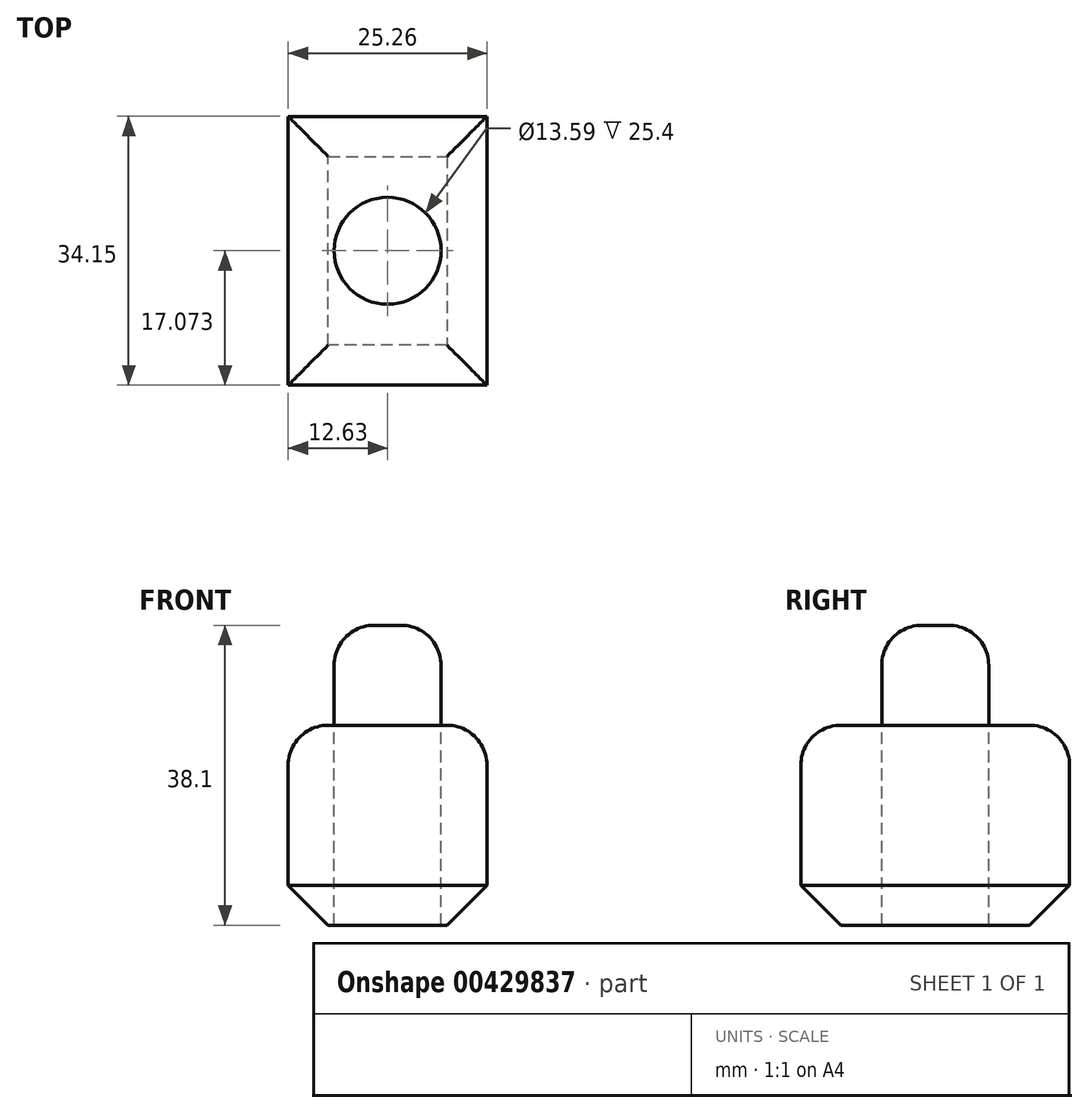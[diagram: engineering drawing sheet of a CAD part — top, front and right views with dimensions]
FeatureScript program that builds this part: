
annotation { "Feature Type Name" : "Feature", "Feature Type Description" : "" }
export const myFeature = defineFeature(function(context is Context, id is Id, definition is map)
    precondition{}
    {
        {
            var Q0;
            Q0=qCreatedBy(makeId("Top.planeOp"),FACE);
            var sketch = newSketch(context, id + "F0", { "sketchPlane" : qUnion([Q0])});
            skLineSegment(sketch, "E0", {"start": v(0, 0) * mm, "end": v(0, 34.15) * mm});
            skLineSegment(sketch, "E1", {"start": v(0, 34.15) * mm, "end": v(25.26, 34.15) * mm});
            skLineSegment(sketch, "E2", {"start": v(25.26, 34.15) * mm, "end": v(25.26, 0) * mm});
            skLineSegment(sketch, "E3", {"start": v(25.26, 0) * mm, "end": v(0, 0) * mm});
            skCircle(sketch, "E4", {"center": v(12.63, 17.07) * mm, "radius": 6.8 * mm});
            skPoint(sketch, "E4.centerSnap0", {"position": v(0, 17.07) * mm});
            skPoint(sketch, "E4.centerSnap1", {"position": v(12.63, 34.15) * mm});
            skSolve(sketch);
        }
        {
            var Q0;
            Q0=makeQuery(id+"F0.imprint","IMPRINT",FACE,{"disambiguationData":[TD([[makeQuery(id+"F0.imprint","IMPRINT",EDGE,{"derivedFrom":sQuery(id+"F0.wireOp",EDGE,"E4")}),1.0]])]});
            extrude(context, id + "F1", {"entities" : qUnion([Q0]), "depth" : 12.7 * mm});
        }
        {
            var Q0;
            Q0=makeQuery(id+"F0.imprint","IMPRINT",FACE,{"disambiguationData":[TD([[makeQuery(id+"F0.imprint","IMPRINT",EDGE,{"derivedFrom":sQuery(id+"F0.wireOp",EDGE,"E0")}),-1.0]])]});
            extrude(context, id + "F2", {"entities" : qUnion([Q0]), "depth" : -25.4 * mm});
        }
        {
            var Q0;
            Q0=makeQuery(id+"F1.opExtrude","CAP_EDGE",EDGE,{"disambiguationData":[OSD([sQuery(id+"F0.wireOp",EDGE,"E4")])],"isStart":false});
            var Q1;
            Q1=makeQuery(id+"F2.opExtrude","CAP_EDGE",EDGE,{"disambiguationData":[OSD([sQuery(id+"F0.wireOp",EDGE,"E2")])],"isStart":true});
            var Q2;
            Q2=makeQuery(id+"F2.opExtrude","CAP_EDGE",EDGE,{"disambiguationData":[OSD([sQuery(id+"F0.wireOp",EDGE,"E1")])],"isStart":true});
            var Q3;
            Q3=makeQuery(id+"F2.opExtrude","CAP_EDGE",EDGE,{"disambiguationData":[OSD([sQuery(id+"F0.wireOp",EDGE,"E0")])],"isStart":true});
            var Q4;
            Q4=makeQuery(id+"F2.opExtrude","CAP_EDGE",EDGE,{"disambiguationData":[OSD([sQuery(id+"F0.wireOp",EDGE,"E3")])],"isStart":true});
            fillet(context, id + "F3", {"entities" : qUnion([Q0, Q1, Q2, Q3, Q4]), "radius" : 5.08 * mm, "tangentPropagation" : true, "allowEdgeOverflow" : false});
        }
        {
            var Q0;
            Q0=makeQuery(id+"F2.opExtrude","CAP_EDGE",EDGE,{"disambiguationData":[OSD([sQuery(id+"F0.wireOp",EDGE,"E0")])],"isStart":false});
            var Q1;
            Q1=makeQuery(id+"F2.opExtrude","CAP_EDGE",EDGE,{"disambiguationData":[OSD([sQuery(id+"F0.wireOp",EDGE,"E1")])],"isStart":false});
            var Q2;
            Q2=makeQuery(id+"F2.opExtrude","CAP_EDGE",EDGE,{"disambiguationData":[OSD([sQuery(id+"F0.wireOp",EDGE,"E2")])],"isStart":false});
            var Q3;
            Q3=makeQuery(id+"F2.opExtrude","CAP_EDGE",EDGE,{"disambiguationData":[OSD([sQuery(id+"F0.wireOp",EDGE,"E3")])],"isStart":false});
            chamfer(context, id + "F4", {"entities" : qUnion([Q0, Q1, Q2, Q3]), "width" : 5.08 * mm, "tangentPropagation" : true});
        }
    });
